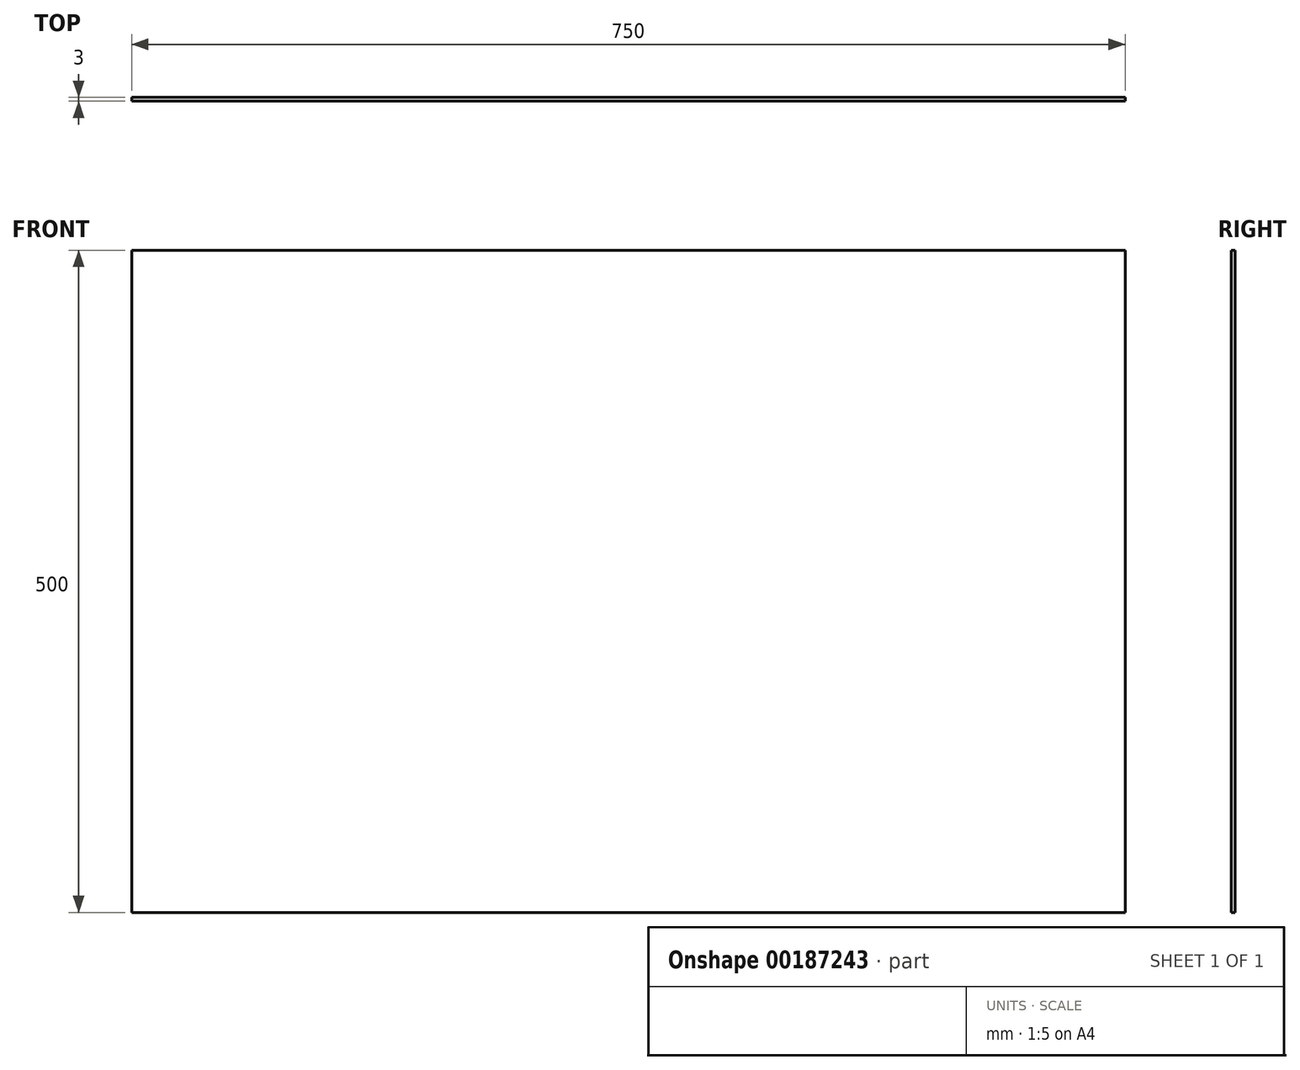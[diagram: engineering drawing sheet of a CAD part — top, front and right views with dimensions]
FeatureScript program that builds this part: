
annotation { "Feature Type Name" : "Feature", "Feature Type Description" : "" }
export const myFeature = defineFeature(function(context is Context, id is Id, definition is map)
    precondition{}
    {
        {
            var Q0;
            Q0=qCreatedBy(makeId("Front.planeOp"),FACE);
            var sketch = newSketch(context, id + "F0", { "sketchPlane" : qUnion([Q0])});
            skLineSegment(sketch, "E0.bottom", {"start": v(-375, 250) * mm, "end": v(375, 250) * mm});
            skLineSegment(sketch, "E0.top", {"start": v(-375, -250) * mm, "end": v(375, -250) * mm});
            skLineSegment(sketch, "E0.left", {"start": v(-375, 250) * mm, "end": v(-375, -250) * mm});
            skLineSegment(sketch, "E0.right", {"start": v(375, 250) * mm, "end": v(375, -250) * mm});
            skPoint(sketch, "E0.middle", {"position": v(0, 0) * mm});
            skSolve(sketch);
        }
        {
            var Q0;
            Q0=makeQuery(id+"F0.imprint","IMPRINT",FACE,{"disambiguationData":[TD([[makeQuery(id+"F0.imprint","IMPRINT",EDGE,{"derivedFrom":sQuery(id+"F0.wireOp",EDGE,"E0.bottom")}),-1.0]])]});
            extrude(context, id + "F1", {"entities" : qUnion([Q0]), "depth" : 3 * mm});
        }
    });
